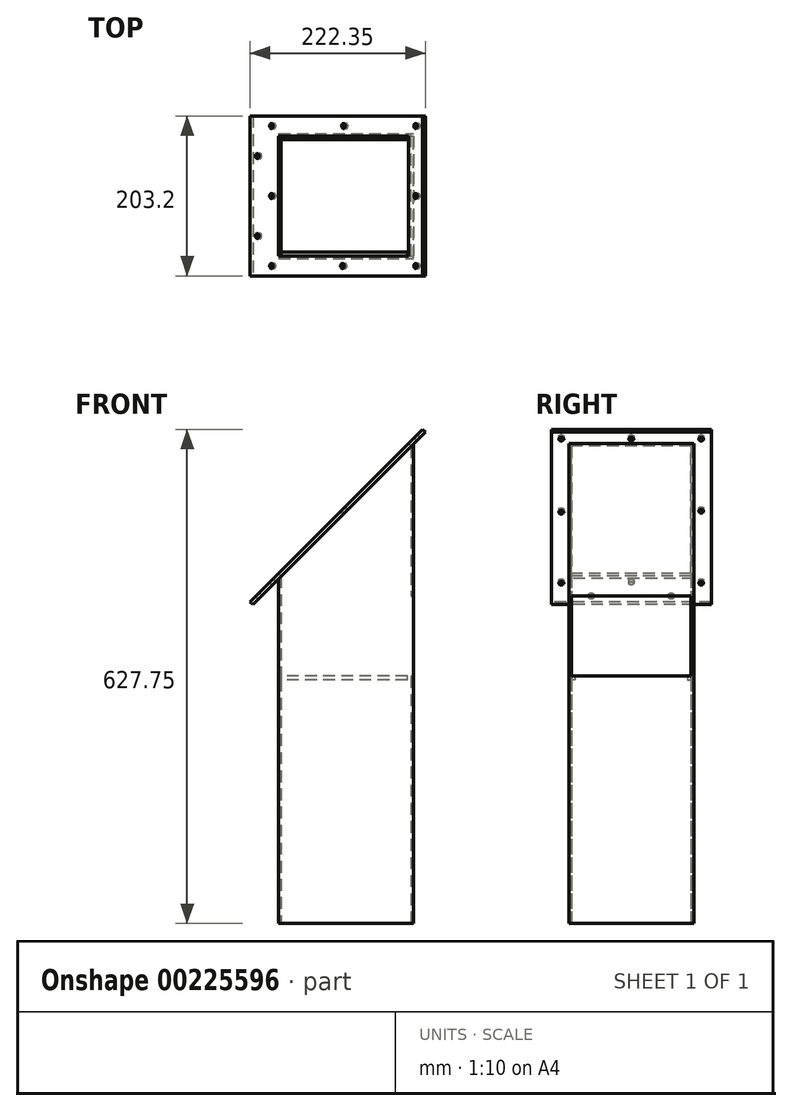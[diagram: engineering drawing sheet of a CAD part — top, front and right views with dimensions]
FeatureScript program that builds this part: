
annotation { "Feature Type Name" : "Feature", "Feature Type Description" : "" }
export const myFeature = defineFeature(function(context is Context, id is Id, definition is map)
    precondition{}
    {
        {
            var Q0;
            Q0=qCreatedBy(makeId("Top.planeOp"),FACE);
            var sketch = newSketch(context, id + "F0", { "sketchPlane" : qUnion([Q0])});
            skLineSegment(sketch, "E0.bottom", {"start": v(82.55, -76.2) * mm, "end": v(-82.55, -76.2) * mm});
            skLineSegment(sketch, "E0.top", {"start": v(82.55, 76.2) * mm, "end": v(-82.55, 76.2) * mm});
            skLineSegment(sketch, "E0.left", {"start": v(82.55, -76.2) * mm, "end": v(82.55, 76.2) * mm});
            skLineSegment(sketch, "E0.right", {"start": v(-82.55, -76.2) * mm, "end": v(-82.55, 76.2) * mm});
            skPoint(sketch, "E0.middle", {"position": v(0, 0) * mm});
            skLineSegment(sketch, "E1.0", {"start": v(-85.73, -79.38) * mm, "end": v(-85.73, 79.37) * mm});
            skLineSegment(sketch, "E1.1", {"start": v(85.73, -79.37) * mm, "end": v(-85.73, -79.38) * mm});
            skLineSegment(sketch, "E1.2", {"start": v(85.73, -79.37) * mm, "end": v(85.72, 79.38) * mm});
            skLineSegment(sketch, "E1.3", {"start": v(85.72, 79.38) * mm, "end": v(-85.73, 79.37) * mm});
            skSolve(sketch);
        }
        {
            var Q0;
            Q0=qSketchRegion(id+"F0",true);
            extrude(context, id + "F1", {"entities" : qUnion([Q0]), "depth" : 609.6 * mm});
        }
        {
            var Q0;
            Q0=makeQuery(id+"F1.opExtrude","SWEPT_FACE",FACE,{"disambiguationData":[OSD([sQuery(id+"F0.wireOp",EDGE,"E1.1")])]});
            var sketch = newSketch(context, id + "F2", { "sketchPlane" : qUnion([Q0])});
            skLineSegment(sketch, "E2", {"start": v(85.72, 609.6) * mm, "end": v(-85.73, 609.6) * mm});
            skLineSegment(sketch, "E3", {"start": v(-85.73, 609.6) * mm, "end": v(-85.73, 438.15) * mm});
            skLineSegment(sketch, "E4", {"start": v(-85.73, 438.15) * mm, "end": v(85.72, 609.6) * mm});
            skSolve(sketch);
        }
        {
            var Q0;
            Q0=qSketchRegion(id+"F2",true);
            extrude(context, id + "F3", {"entities" : qUnion([Q0]), "operationType" : NewBodyOperationType.REMOVE, "endBound" : BoundingType.THROUGH_ALL, "oppositeDirection" : true, "depth" : 25.4 * mm});
        }
        {
            var Q0;
            Q0=makeQuery(id+"F3.boolean.opBoolean","COPY",FACE,{"derivedFrom":makeQuery(id+"F3.opExtrude","SWEPT_FACE",FACE,{"disambiguationData":[OSD([sQuery(id+"F2.wireOp",EDGE,"E4")])]})});
            var sketch = newSketch(context, id + "F4", { "sketchPlane" : qUnion([Q0])});
            skLineSegment(sketch, "E5.0", {"start": v(-76.2, 253.7) * mm, "end": v(-76.2, 487.18) * mm});
            skLineSegment(sketch, "E6.0", {"start": v(-76.2, 487.18) * mm, "end": v(76.2, 487.18) * mm});
            skLineSegment(sketch, "E7.0", {"start": v(76.2, 253.7) * mm, "end": v(76.2, 487.18) * mm});
            skLineSegment(sketch, "E8.0", {"start": v(-76.2, 253.7) * mm, "end": v(76.2, 253.7) * mm});
            skLineSegment(sketch, "E9.0", {"start": v(-101.6, 228.3) * mm, "end": v(-101.6, 512.58) * mm});
            skLineSegment(sketch, "E9.1", {"start": v(-101.6, 228.3) * mm, "end": v(101.6, 228.3) * mm});
            skLineSegment(sketch, "E9.2", {"start": v(101.6, 228.3) * mm, "end": v(101.6, 512.58) * mm});
            skLineSegment(sketch, "E9.3", {"start": v(-101.6, 512.58) * mm, "end": v(101.6, 512.58) * mm});
            skLineSegment(sketch, "E10.top", {"start": v(-101.6, 202.9) * mm, "end": v(101.6, 202.9) * mm});
            skLineSegment(sketch, "E10.left", {"start": v(-101.6, 228.3) * mm, "end": v(-101.6, 202.9) * mm});
            skLineSegment(sketch, "E10.right", {"start": v(101.6, 228.3) * mm, "end": v(101.6, 202.9) * mm});
            skCircle(sketch, "E11", {"center": v(-50.8, 215.6) * mm, "radius": 3.18 * mm});
            skPoint(sketch, "E11.centerSnap0", {"position": v(-101.6, 215.6) * mm});
            skCircle(sketch, "E12", {"center": v(50.8, 215.6) * mm, "radius": 3.18 * mm});
            skPoint(sketch, "E12.centerSnap0", {"position": v(101.6, 215.6) * mm});
            skCircle(sketch, "E13", {"center": v(0, 241) * mm, "radius": 3.18 * mm});
            skCircle(sketch, "E14", {"center": v(0, 499.88) * mm, "radius": 3.18 * mm});
            skPoint(sketch, "E14.centerSnap0", {"position": v(0, 512.58) * mm});
            skCircle(sketch, "E15", {"center": v(88.9, 499.88) * mm, "radius": 3.18 * mm});
            skCircle(sketch, "E16", {"center": v(-88.9, 499.88) * mm, "radius": 3.18 * mm});
            skCircle(sketch, "E17", {"center": v(-88.9, 370.44) * mm, "radius": 3.18 * mm});
            skPoint(sketch, "E17.centerSnap0", {"position": v(-101.6, 370.44) * mm});
            skCircle(sketch, "E18", {"center": v(-88.9, 241) * mm, "radius": 3.18 * mm});
            skCircle(sketch, "E19", {"center": v(88.9, 241) * mm, "radius": 3.18 * mm});
            skCircle(sketch, "E20", {"center": v(88.9, 368.56) * mm, "radius": 3.18 * mm});
            skSolve(sketch);
        }
        {
            var Q0;
            Q0=qSketchRegion(id+"F4",true);
            extrude(context, id + "F5", {"entities" : qUnion([Q0]), "operationType" : NewBodyOperationType.ADD, "depth" : 4.76 * mm});
        }
        {
            var Q0;
            Q0=makeQuery(id+"F1.opExtrude","SWEPT_FACE",FACE,{"disambiguationData":[OSD([sQuery(id+"F0.wireOp",EDGE,"E1.2")])]});
            var sketch = newSketch(context, id + "F6", { "sketchPlane" : qUnion([Q0])});
            skLineSegment(sketch, "E21.0", {"start": v(76.2, 441.32) * mm, "end": v(-76.2, 441.32) * mm, "construction": true});
            skLineSegment(sketch, "E22.0", {"start": v(76.2, 415.93) * mm, "end": v(-76.2, 415.93) * mm});
            skLineSegment(sketch, "E23", {"start": v(-76.2, 415.93) * mm, "end": v(-76.2, 314.32) * mm});
            skLineSegment(sketch, "E24", {"start": v(-76.2, 314.32) * mm, "end": v(76.2, 314.32) * mm});
            skLineSegment(sketch, "E25", {"start": v(76.2, 314.32) * mm, "end": v(76.2, 415.93) * mm});
            skSolve(sketch);
        }
        {
            var Q0;
            Q0=qSketchRegion(id+"F6",true);
            extrude(context, id + "F7", {"entities" : qUnion([Q0]), "operationType" : NewBodyOperationType.REMOVE, "oppositeDirection" : true, "depth" : 25.4 * mm});
        }
        {
            var Q0;
            Q0=makeQuery(id+"F7.boolean.opBoolean","MERGE",FACE,{"derivedFrom":[makeQuery(id+"F5.boolean.opBoolean","MERGE",FACE,{"derivedFrom":[makeQuery(id+"F1.opExtrude","SWEPT_FACE",FACE,{"disambiguationData":[OSD([sQuery(id+"F0.wireOp",EDGE,"E0.bottom")])]}),makeQuery(id+"F5.opExtrude","SWEPT_FACE",FACE,{"disambiguationData":[OSD([sQuery(id+"F4.wireOp",EDGE,"E7.0")])]})]}),makeQuery(id+"F7.opExtrude","SWEPT_FACE",FACE,{"disambiguationData":[OSD([sQuery(id+"F6.wireOp",EDGE,"E23")])]})]});
            var sketch = newSketch(context, id + "F8", { "sketchPlane" : qUnion([Q0])});
            skLineSegment(sketch, "E26.0", {"start": v(-82.55, 314.32) * mm, "end": v(-85.72, 314.32) * mm});
            skLineSegment(sketch, "E27.bottom", {"start": v(-82.55, 314.32) * mm, "end": v(82.55, 314.32) * mm});
            skLineSegment(sketch, "E27.top", {"start": v(-82.55, 309.56) * mm, "end": v(82.55, 309.56) * mm});
            skLineSegment(sketch, "E27.left", {"start": v(-82.55, 314.32) * mm, "end": v(-82.55, 309.56) * mm});
            skLineSegment(sketch, "E27.right", {"start": v(82.55, 314.32) * mm, "end": v(82.55, 309.56) * mm});
            skLineSegment(sketch, "E28", {"start": v(-77.79, 314.32) * mm, "end": v(-77.79, 309.56) * mm});
            skSolve(sketch);
        }
        {
            var Q0;
            {var subQ0=sQuery(id+"F8.wireOp",EDGE,"E27.right");Q0=makeQuery(id+"F8.imprint","IMPRINT",FACE,{"disambiguationData":[TD([[makeQuery(id+"F8.imprint","IMPRINT",EDGE,{"derivedFrom":subQ0}),-1.0]])]});}
            extrude(context, id + "F9", {"entities" : qUnion([Q0]), "operationType" : NewBodyOperationType.ADD, "depth" : 4.76 * mm});
        }
        {
            var Q0;
            Q0=makeQuery(id+"F7.boolean.opBoolean","MERGE",FACE,{"derivedFrom":[makeQuery(id+"F5.boolean.opBoolean","MERGE",FACE,{"derivedFrom":[makeQuery(id+"F1.opExtrude","SWEPT_FACE",FACE,{"disambiguationData":[OSD([sQuery(id+"F0.wireOp",EDGE,"E0.top")])]}),makeQuery(id+"F5.opExtrude","SWEPT_FACE",FACE,{"disambiguationData":[OSD([sQuery(id+"F4.wireOp",EDGE,"E5.0")])]})]}),makeQuery(id+"F7.opExtrude","SWEPT_FACE",FACE,{"disambiguationData":[OSD([sQuery(id+"F6.wireOp",EDGE,"E25")])]})]});
            var sketch = newSketch(context, id + "F10", { "sketchPlane" : qUnion([Q0])});
            skLineSegment(sketch, "E29.0", {"start": v(82.55, 314.32) * mm, "end": v(85.72, 314.32) * mm});
            skLineSegment(sketch, "E30.bottom", {"start": v(82.55, 314.32) * mm, "end": v(-82.55, 314.32) * mm});
            skLineSegment(sketch, "E30.top", {"start": v(82.55, 309.56) * mm, "end": v(-82.55, 309.56) * mm});
            skLineSegment(sketch, "E30.left", {"start": v(82.55, 314.32) * mm, "end": v(82.55, 309.56) * mm});
            skLineSegment(sketch, "E30.right", {"start": v(-82.55, 314.32) * mm, "end": v(-82.55, 309.56) * mm});
            skLineSegment(sketch, "E31", {"start": v(77.79, 309.56) * mm, "end": v(77.79, 314.32) * mm});
            skPoint(sketch, "E31.endSnap0", {"position": v(84.14, 314.32) * mm});
            skSolve(sketch);
        }
        {
            var Q0;
            {var subQ0=sQuery(id+"F10.wireOp",EDGE,"E30.right");Q0=makeQuery(id+"F10.imprint","IMPRINT",FACE,{"disambiguationData":[TD([[makeQuery(id+"F10.imprint","IMPRINT",EDGE,{"derivedFrom":subQ0}),1.0]])]});}
            extrude(context, id + "F11", {"entities" : qUnion([Q0]), "operationType" : NewBodyOperationType.ADD, "depth" : 4.76 * mm});
        }
    });
